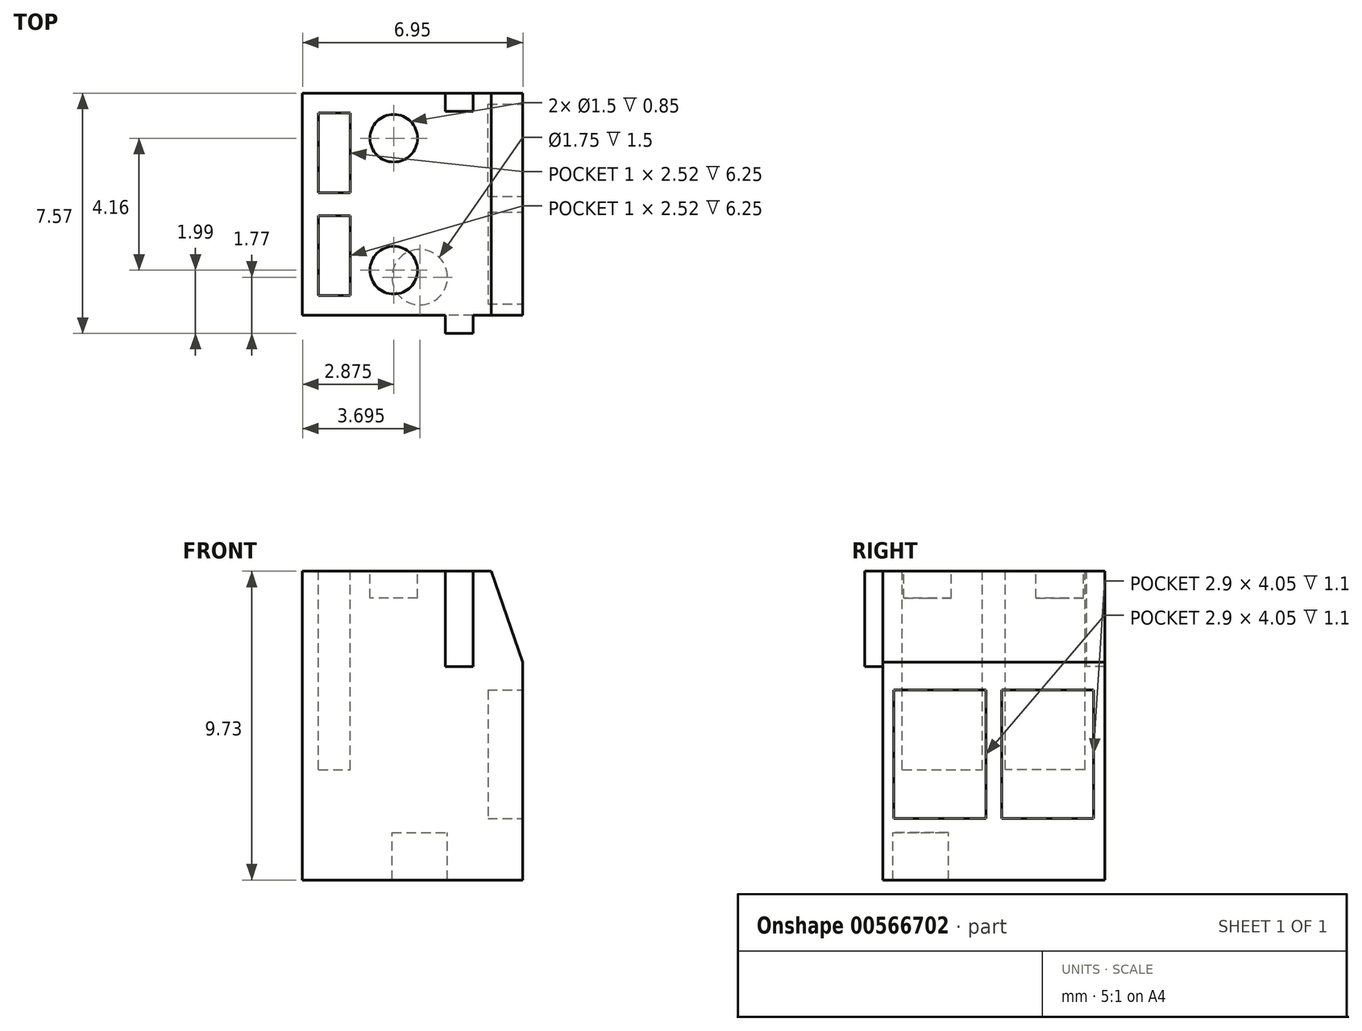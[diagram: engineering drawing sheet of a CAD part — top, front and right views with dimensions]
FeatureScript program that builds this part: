
annotation { "Feature Type Name" : "Feature", "Feature Type Description" : "" }
export const myFeature = defineFeature(function(context is Context, id is Id, definition is map)
    precondition{}
    {
        {
            var Q0;
            Q0=qCreatedBy(makeId("Top.planeOp"),FACE);
            var sketch = newSketch(context, id + "F0", { "sketchPlane" : qUnion([Q0])});
            skLineSegment(sketch, "E0.bottom", {"start": v(3.47, 3.5) * mm, "end": v(-3.48, 3.5) * mm});
            skLineSegment(sketch, "E0.top", {"start": v(3.48, -3.5) * mm, "end": v(-3.47, -3.5) * mm});
            skLineSegment(sketch, "E0.left", {"start": v(3.47, 3.5) * mm, "end": v(3.48, -3.5) * mm});
            skLineSegment(sketch, "E0.right", {"start": v(-3.48, 3.5) * mm, "end": v(-3.47, -3.5) * mm});
            skPoint(sketch, "E0.middle", {"position": v(0, 0) * mm});
            skSolve(sketch);
        }
        {
            var Q0;
            Q0=makeQuery(id+"F0.imprint","IMPRINT",FACE,{"disambiguationData":[TD([[makeQuery(id+"F0.imprint","IMPRINT",EDGE,{"derivedFrom":sQuery(id+"F0.wireOp",EDGE,"E0.bottom")}),1.0]])]});
            extrude(context, id + "F1", {"entities" : qUnion([Q0]), "depth" : 8.23 * mm, "offsetDistance" : 25 * mm});
        }
        {
            var Q0;
            Q0=makeQuery(id+"F1.opExtrude","SWEPT_FACE",FACE,{"disambiguationData":[OSD([sQuery(id+"F0.wireOp",EDGE,"E0.top")])]});
            var sketch = newSketch(context, id + "F2", { "sketchPlane" : qUnion([Q0])});
            skLineSegment(sketch, "E1", {"start": v(2.48, 8.23) * mm, "end": v(3.48, 5.37) * mm});
            skLineSegment(sketch, "E2", {"start": v(3.48, 5.37) * mm, "end": v(3.48, 8.23) * mm});
            skLineSegment(sketch, "E3", {"start": v(3.48, 8.23) * mm, "end": v(2.48, 8.23) * mm});
            skSolve(sketch);
        }
        {
            var Q0;
            Q0 = qSketchRegion(id + "F2", true);
            extrude(context, id + "F3", {"entities" : qUnion([Q0]), "operationType" : NewBodyOperationType.REMOVE, "endBound" : BoundingType.THROUGH_ALL, "oppositeDirection" : true, "depth" : 25 * mm, "offsetDistance" : 25 * mm});
        }
        {
            var Q0;
            Q0=makeQuery(id+"F1.opExtrude","SWEPT_FACE",FACE,{"disambiguationData":[OSD([sQuery(id+"F0.wireOp",EDGE,"E0.left")])]});
            var sketch = newSketch(context, id + "F4", { "sketchPlane" : qUnion([Q0])});
            skLineSegment(sketch, "E4.bottom", {"start": v(-0.25, 4.49) * mm, "end": v(-3.15, 4.49) * mm});
            skLineSegment(sketch, "E4.top", {"start": v(-0.25, 0.44) * mm, "end": v(-3.15, 0.44) * mm});
            skLineSegment(sketch, "E4.left", {"start": v(-0.25, 4.49) * mm, "end": v(-0.25, 0.44) * mm});
            skLineSegment(sketch, "E4.right", {"start": v(-3.15, 4.49) * mm, "end": v(-3.15, 0.44) * mm});
            skPoint(sketch, "E4.middle", {"position": v(-1.7, 2.46) * mm});
            skLineSegment(sketch, "E5.MirrorCS", {"start": v(3.15, 4.49) * mm, "end": v(3.15, 0.44) * mm});
            skLineSegment(sketch, "E6.MirrorCS", {"start": v(0.25, 4.49) * mm, "end": v(0.25, 0.44) * mm});
            skLineSegment(sketch, "E7.MirrorCS", {"start": v(0.25, 4.49) * mm, "end": v(3.15, 4.49) * mm});
            skLineSegment(sketch, "E8.MirrorCS", {"start": v(0.25, 0.44) * mm, "end": v(3.15, 0.44) * mm});
            skPoint(sketch, "E9.MirrorP", {"position": v(1.7, 2.46) * mm});
            skSolve(sketch);
        }
        {
            var Q0;
            Q0 = qSketchRegion(id + "F4", true);
            extrude(context, id + "F5", {"entities" : qUnion([Q0]), "operationType" : NewBodyOperationType.REMOVE, "oppositeDirection" : true, "depth" : 1.1 * mm, "offsetDistance" : 25 * mm});
        }
        {
            var Q0;
            Q0=makeQuery(id+"F1.opExtrude","CAP_FACE",FACE,{"disambiguationData":[OSD([sQuery(id+"F0.wireOp",EDGE,"E0.bottom"),sQuery(id+"F0.wireOp",EDGE,"E0.top"),sQuery(id+"F0.wireOp",EDGE,"E0.left"),sQuery(id+"F0.wireOp",EDGE,"E0.right")])],"isStart":false});
            var sketch = newSketch(context, id + "F6", { "sketchPlane" : qUnion([Q0])});
            skLineSegment(sketch, "E10.bottom", {"start": v(1.04, -3.5) * mm, "end": v(1.9, -3.5) * mm});
            skLineSegment(sketch, "E10.top", {"start": v(1.04, -4.07) * mm, "end": v(1.9, -4.07) * mm});
            skLineSegment(sketch, "E10.left", {"start": v(1.04, -3.5) * mm, "end": v(1.04, -4.07) * mm});
            skLineSegment(sketch, "E10.right", {"start": v(1.9, -3.5) * mm, "end": v(1.9, -4.07) * mm});
            skSolve(sketch);
        }
        {
            var Q0;
            Q0=makeQuery(id+"F6.imprint","IMPRINT",FACE,{"disambiguationData":[TD([[makeQuery(id+"F6.imprint","IMPRINT",EDGE,{"derivedFrom":sQuery(id+"F6.wireOp",EDGE,"E10.bottom")}),1.0]])]});
            var Q1;
            Q1=makeQuery(id+"F1.opExtrude","CAP_FACE",FACE,{"disambiguationData":[OSD([sQuery(id+"F0.wireOp",EDGE,"E0.bottom"),sQuery(id+"F0.wireOp",EDGE,"E0.top"),sQuery(id+"F0.wireOp",EDGE,"E0.left"),sQuery(id+"F0.wireOp",EDGE,"E0.right")])],"isStart":true});
            extrude(context, id + "F7", {"entities" : qUnion([Q0]), "operationType" : NewBodyOperationType.ADD, "oppositeDirection" : true, "depth" : 3 * mm, "endBoundEntityFace" : qUnion([Q1]), "offsetDistance" : 25 * mm});
        }
        {
            var Q0;
            Q0=makeQuery(id+"F7.boolean.opBoolean","MERGE",FACE,{"derivedFrom":[makeQuery(id+"F1.opExtrude","CAP_FACE",FACE,{"disambiguationData":[OSD([sQuery(id+"F0.wireOp",EDGE,"E0.bottom"),sQuery(id+"F0.wireOp",EDGE,"E0.top"),sQuery(id+"F0.wireOp",EDGE,"E0.left"),sQuery(id+"F0.wireOp",EDGE,"E0.right")])],"isStart":false}),makeQuery(id+"F7.opExtrude","CAP_FACE",FACE,{"disambiguationData":[OSD([sQuery(id+"F6.wireOp",EDGE,"E10.bottom"),sQuery(id+"F6.wireOp",EDGE,"E10.top"),sQuery(id+"F6.wireOp",EDGE,"E10.left"),sQuery(id+"F6.wireOp",EDGE,"E10.right")])],"isStart":true})]});
            var sketch = newSketch(context, id + "F8", { "sketchPlane" : qUnion([Q0])});
            skLineSegment(sketch, "E11.bottom", {"start": v(1.04, 3.5) * mm, "end": v(1.9, 3.5) * mm});
            skLineSegment(sketch, "E11.top", {"start": v(1.04, 2.93) * mm, "end": v(1.9, 2.93) * mm});
            skLineSegment(sketch, "E11.left", {"start": v(1.04, 3.5) * mm, "end": v(1.04, 2.93) * mm});
            skLineSegment(sketch, "E11.right", {"start": v(1.9, 3.5) * mm, "end": v(1.9, 2.93) * mm});
            skSolve(sketch);
        }
        {
            var Q0;
            Q0=makeQuery(id+"F8.imprint","IMPRINT",FACE,{"disambiguationData":[TD([[makeQuery(id+"F8.imprint","IMPRINT",EDGE,{"derivedFrom":sQuery(id+"F8.wireOp",EDGE,"E11.bottom")}),1.0]])]});
            extrude(context, id + "F9", {"entities" : qUnion([Q0]), "operationType" : NewBodyOperationType.REMOVE, "oppositeDirection" : true, "depth" : 3 * mm, "offsetDistance" : 25 * mm});
        }
        {
            var Q0;
            Q0=makeQuery(id+"F7.boolean.opBoolean","MERGE",FACE,{"derivedFrom":[makeQuery(id+"F1.opExtrude","CAP_FACE",FACE,{"disambiguationData":[OSD([sQuery(id+"F0.wireOp",EDGE,"E0.bottom"),sQuery(id+"F0.wireOp",EDGE,"E0.top"),sQuery(id+"F0.wireOp",EDGE,"E0.left"),sQuery(id+"F0.wireOp",EDGE,"E0.right")])],"isStart":false}),makeQuery(id+"F7.opExtrude","CAP_FACE",FACE,{"disambiguationData":[OSD([sQuery(id+"F6.wireOp",EDGE,"E10.bottom"),sQuery(id+"F6.wireOp",EDGE,"E10.top"),sQuery(id+"F6.wireOp",EDGE,"E10.left"),sQuery(id+"F6.wireOp",EDGE,"E10.right")])],"isStart":true})]});
            var sketch = newSketch(context, id + "F10", { "sketchPlane" : qUnion([Q0])});
            skCircle(sketch, "E12", {"center": v(-0.6, -2.08) * mm, "radius": 0.75 * mm});
            skCircle(sketch, "E13.MirrorC", {"center": v(-0.6, 2.08) * mm, "radius": 0.75 * mm});
            skSolve(sketch);
        }
        {
            var Q0;
            Q0 = qSketchRegion(id + "F10", true);
            extrude(context, id + "F11", {"entities" : qUnion([Q0]), "operationType" : NewBodyOperationType.REMOVE, "oppositeDirection" : true, "depth" : .85 * mm, "offsetDistance" : 25 * mm});
        }
        {
            var Q0;
            Q0=makeQuery(id+"F7.boolean.opBoolean","MERGE",FACE,{"derivedFrom":[makeQuery(id+"F1.opExtrude","CAP_FACE",FACE,{"disambiguationData":[OSD([sQuery(id+"F0.wireOp",EDGE,"E0.bottom"),sQuery(id+"F0.wireOp",EDGE,"E0.top"),sQuery(id+"F0.wireOp",EDGE,"E0.left"),sQuery(id+"F0.wireOp",EDGE,"E0.right")])],"isStart":false}),makeQuery(id+"F7.opExtrude","CAP_FACE",FACE,{"disambiguationData":[OSD([sQuery(id+"F6.wireOp",EDGE,"E10.bottom"),sQuery(id+"F6.wireOp",EDGE,"E10.top"),sQuery(id+"F6.wireOp",EDGE,"E10.left"),sQuery(id+"F6.wireOp",EDGE,"E10.right")])],"isStart":true})]});
            var sketch = newSketch(context, id + "F12", { "sketchPlane" : qUnion([Q0])});
            skLineSegment(sketch, "E14.bottom", {"start": v(-2.96, -2.88) * mm, "end": v(-1.96, -2.88) * mm});
            skLineSegment(sketch, "E14.top", {"start": v(-2.96, -0.36) * mm, "end": v(-1.96, -0.36) * mm});
            skLineSegment(sketch, "E14.left", {"start": v(-2.96, -2.88) * mm, "end": v(-2.97, -0.36) * mm});
            skLineSegment(sketch, "E14.right", {"start": v(-1.96, -2.88) * mm, "end": v(-1.96, -0.36) * mm});
            skLineSegment(sketch, "E15.MirrorCS", {"start": v(-2.96, 0.36) * mm, "end": v(-1.96, 0.36) * mm});
            skLineSegment(sketch, "E16.MirrorCS", {"start": v(-1.96, 2.88) * mm, "end": v(-1.96, 0.36) * mm});
            skLineSegment(sketch, "E17.MirrorCS", {"start": v(-2.96, 2.88) * mm, "end": v(-2.97, 0.36) * mm});
            skLineSegment(sketch, "E18.MirrorCS", {"start": v(-2.96, 2.88) * mm, "end": v(-1.96, 2.88) * mm});
            skSolve(sketch);
        }
        {
            var Q0;
            Q0=makeQuery(id+"F12.imprint","IMPRINT",FACE,{"disambiguationData":[TD([[makeQuery(id+"F12.imprint","IMPRINT",EDGE,{"derivedFrom":sQuery(id+"F12.wireOp",EDGE,"E14.bottom")}),1.0]])]});
            var Q1;
            Q1=makeQuery(id+"F12.imprint","IMPRINT",FACE,{"disambiguationData":[TD([[makeQuery(id+"F12.imprint","IMPRINT",EDGE,{"derivedFrom":sQuery(id+"F12.wireOp",EDGE,"E16.MirrorCS")}),-1.0]])]});
            extrude(context, id + "F13", {"entities" : qUnion([Q0, Q1]), "operationType" : NewBodyOperationType.REMOVE, "oppositeDirection" : true, "depth" : 6.25 * mm, "offsetDistance" : 25 * mm});
        }
        {
            var Q0;
            Q0=makeQuery(id+"F1.opExtrude","CAP_FACE",FACE,{"disambiguationData":[OSD([sQuery(id+"F0.wireOp",EDGE,"E0.bottom"),sQuery(id+"F0.wireOp",EDGE,"E0.top"),sQuery(id+"F0.wireOp",EDGE,"E0.left"),sQuery(id+"F0.wireOp",EDGE,"E0.right")])],"isStart":true});
            var sketch = newSketch(context, id + "F14", { "sketchPlane" : qUnion([Q0])});
            skCircle(sketch, "E19", {"center": v(0.22, -2.3) * mm, "radius": 0.88 * mm});
            skCircle(sketch, "E20.MirrorC", {"center": v(0.22, 2.3) * mm, "radius": 0.88 * mm});
            skSolve(sketch);
        }
        {
            var Q0;
            Q0=makeQuery(id+"F14.imprint","IMPRINT",FACE,{"disambiguationData":[TD([[makeQuery(id+"F14.imprint","IMPRINT",EDGE,{"derivedFrom":sQuery(id+"F14.wireOp",EDGE,"E20.MirrorC")}),-1.0]])]});
            var Q1;
            Q1=makeQuery(id+"F14.imprint","IMPRINT",FACE,{"disambiguationData":[TD([[makeQuery(id+"F14.imprint","IMPRINT",EDGE,{"derivedFrom":sQuery(id+"F14.wireOp",EDGE,"E19")}),1.0]])]});
            extrude(context, id + "F15", {"entities" : qUnion([Q0, Q1]), "operationType" : NewBodyOperationType.ADD, "depth" : 1.5 * mm, "offsetDistance" : 25 * mm});
        }
    });
